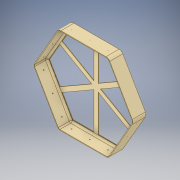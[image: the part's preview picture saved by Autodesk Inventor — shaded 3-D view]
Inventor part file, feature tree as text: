
AUTODESK INVENTOR PART (.ipt)
format: ipt  version: 2019 (Build 230136000, 136)  size: 231,936 bytes
history: native  units: mm
features: mirror x4, extrude x3, sketch x3, plane x3, fillet x2, shell x1, projected_geometry x1
ambient origin geometry x8: Origin, YZ Plane, XZ Plane, XY Plane, X Axis, Y Axis, Z Axis, Center Point
bodies: Solid1 (feature_tree)
feature tree (17):
  extrude  "Extrusion1"  Depth=30.0mm TaperAngle=0.0deg
  shell  "Shell1"  Thickness=1.5mm
  sketch  "Sketch2"  dims[d5=2.0mm d6=15.0mm d7=15.0mm d8=1.0mm d9=0.0mm]
  plane  "Work Plane1"
  plane  "Work Plane2"
  plane  "Work Plane3"
  extrude  "Extrusion2"  Depth=1.0mm
  mirror  "Mirror1"
  mirror  "Mirror2"
  mirror  "Mirror3"
  mirror  "Mirror4"
  fillet  "Fillet1"  Radius=15.0mm
  fillet  "Fillet2"  Radius=1.0mm
  extrude  "Extrusion3"  Depth=10.0mm
  sketch  "Sketch1"  dims[d0=200.0mm d2=30.0mm d3=0.0mm d4=1.5mm]
  projected_geometry  "Projected Loop1"
  sketch  "Sketch3"  dims[d10=4.0mm d11=10.0mm d12=1.0mm d15=10.0mm d16=30.0mm d18=360.0deg d20=10.0mm d21=0.0mm d22=10.0mm]
